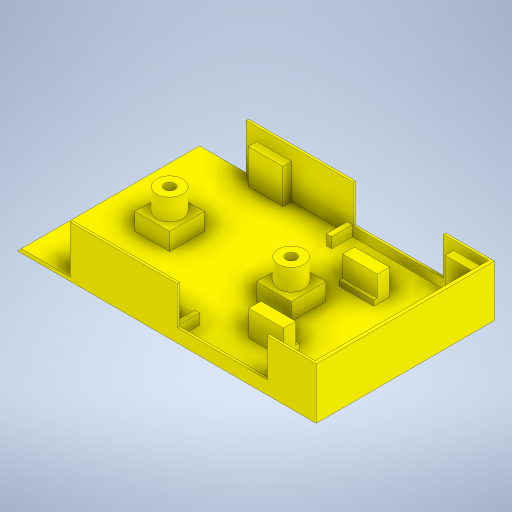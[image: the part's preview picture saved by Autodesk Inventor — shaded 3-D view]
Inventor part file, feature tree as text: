
AUTODESK INVENTOR PART (.ipt)
format: ipt  version: 2024 (Build 280153000, 153)  size: 497,664 bytes
history: native  units: mm
features: extrude x16, sketch x15, mirror x5, chamfer x1
ambient origin geometry x8: Origin, YZ Plane, XZ Plane, XY Plane, X Axis, Y Axis, Z Axis, Center Point
bodies: Solid1 (feature_tree)
feature tree (37):
  extrude  "Extrusion1"  Depth=100.0mm
  sketch  "Sketch2"  dims[d2=2.2mm d3=0.0mm d4=20.0mm]
  extrude  "Extrusion2"  Depth=20.0mm
  extrude  "Extrusion3"  Depth=15.0mm
  extrude  "Extrusion4"  Depth=10.0mm TaperAngle=0.0deg
  extrude  "Extrusion5"  Depth=7.0mm TaperAngle=0.0deg
  extrude  "Extrusion6"  Depth=6.0mm
  extrude  "Extrusion7"  Depth=1.3mm
  extrude  "Extrusion8"  Depth=2.0mm
  extrude  "Extrusion9"  Depth=1.3mm TaperAngle=0.0deg
  extrude  "Extrusion10"  Depth=2.0mm TaperAngle=0.0deg
  extrude  "Extrusion11"  Depth=5.0mm
  mirror  "Mirror1"
  extrude  "Extrusion12"  Depth=5.0mm
  extrude  "Extrusion13"  Depth=27.4mm TaperAngle=0.0deg
  mirror  "Mirror2"
  extrude  "Extrusion14"  Depth=15.0mm TaperAngle=0.0deg
  mirror  "Mirror3"
  extrude  "Extrusion15"  Depth=20.0mm
  mirror  "Mirror4"
  extrude  "Extrusion16"  Depth=2.0mm
  mirror  "Mirror5"
  chamfer  "Chamfer1"  Distance=3.0mm
  sketch  "Sketch1"  dims[d0=170.0mm d1=100.0mm]
  sketch  "Sketch3"  dims[d5=20.0mm d6=15.0mm]
  sketch  "Sketch4"  dims[d7=22.4mm d8=0.0mm d9=10.0mm d10=0.0mm]
  sketch  "Sketch5"  dims[d11=6.0mm d12=7.0mm d13=0.0mm]
  sketch  "Sketch6"  dims[d14=20.0mm d15=20.0mm d16=15.0mm d17=6.0mm]
  sketch  "Sketch7"  dims[d18=7.0mm d19=0.0mm d20=1.3mm]
  sketch  "Sketch8"  dims[d21=1.3mm d22=2.0mm]
  sketch  "Sketch9"  dims[d23=27.4mm d24=0.0mm d25=1.3mm d26=0.0mm]
  sketch  "Sketch10"  dims[d27=1.3mm d28=0.0mm d29=2.0mm d30=0.0mm]
  sketch  "Sketch11"  dims[d31=20.0mm d32=5.0mm]
  sketch  "Sketch12"  dims[d33=20.0mm d34=5.0mm]
  sketch  "Sketch13"  dims[d35=22.4mm d36=0.0mm d37=27.4mm d38=0.0mm]
  sketch  "Sketch14"  dims[d39=7.0mm d40=15.0mm d41=0.0mm]
  sketch  "Sketch15"  dims[d42=19.5mm d43=20.0mm d44=2.0mm d45=3.0mm d46=0.0mm d47=3.0mm d48=12.0mm d49=6.0mm d50=0.0mm d51=20.0mm d52=5.0mm d53=20.0mm d54=0.0mm d55=20.0mm d56=0.0mm d57=2.2mm d58=2.0mm d59=45.0deg]
